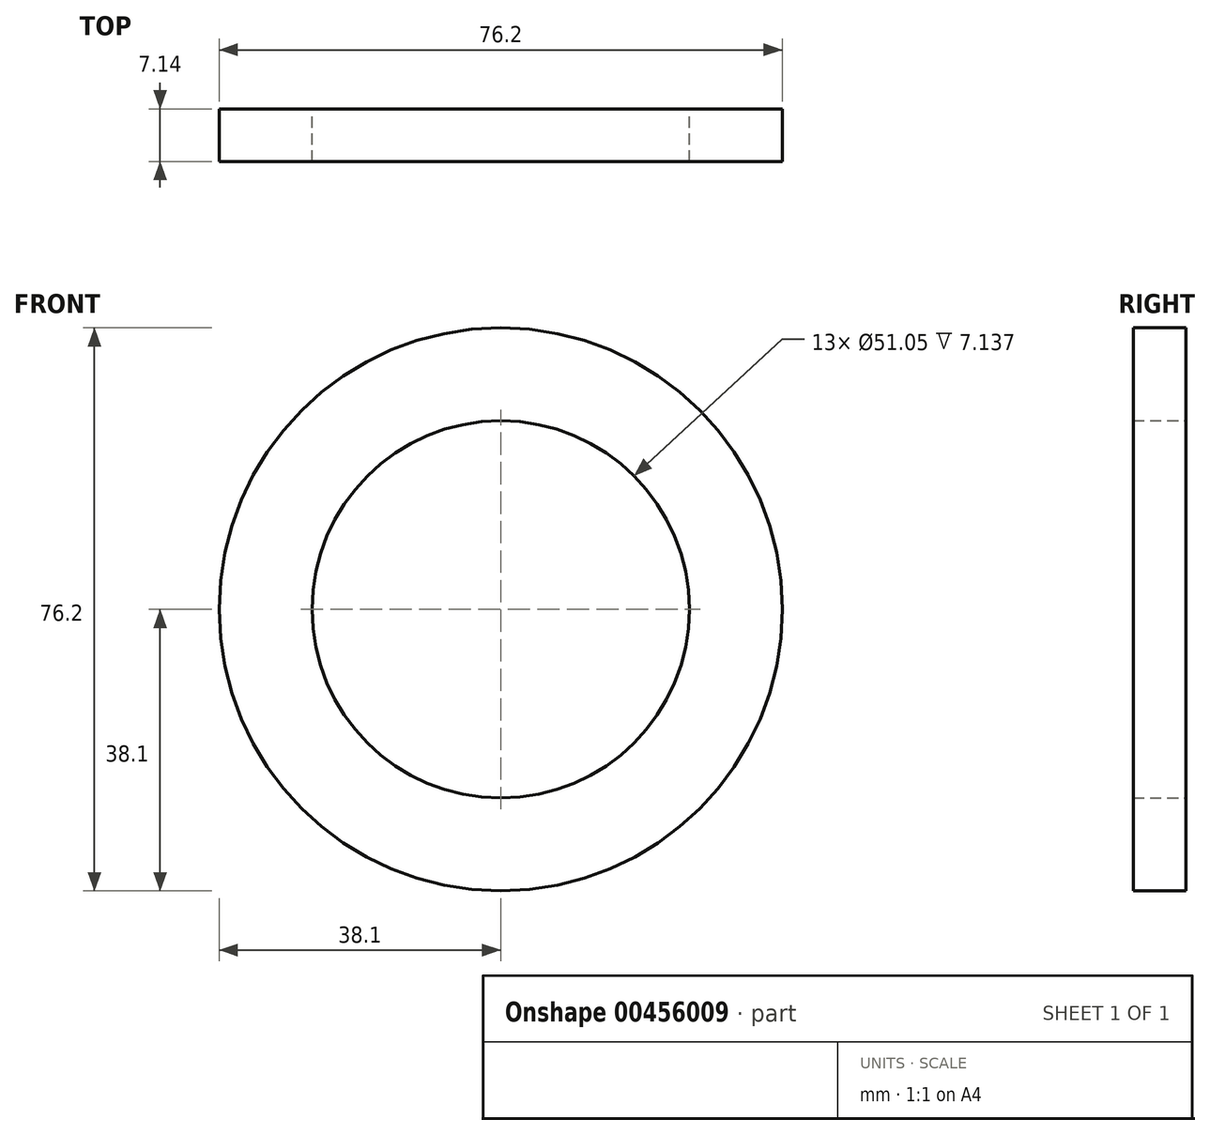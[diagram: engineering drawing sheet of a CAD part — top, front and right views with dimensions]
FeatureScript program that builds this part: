
annotation { "Feature Type Name" : "Feature", "Feature Type Description" : "" }
export const myFeature = defineFeature(function(context is Context, id is Id, definition is map)
    precondition{}
    {
        {
            var Q0;
            Q0=qCreatedBy(makeId("Front.planeOp"),FACE);
            var sketch = newSketch(context, id + "F0", { "sketchPlane" : qUnion([Q0])});
            skCircle(sketch, "E0", {"center": v(0, 0) * mm, "radius": 25.53 * mm});
            skCircle(sketch, "E1", {"center": v(0, 0) * mm, "radius": 38.1 * mm});
            skSolve(sketch);
        }
        {
            var Q0;
            Q0 = qSketchRegion(id + "F0", true);
            extrude(context, id + "F1", {"entities" : qUnion([Q0]), "depth" : 7.14 * mm});
        }
    });
